# Revit family: QF_ELECTROLUXPROFESSIONAL_1LSNST_TD6-37_E
name_source: partatom
category: Attrezzature speciali
units: mm (PartAtom-declared; Revit-internal decimal feet)

## family parameters
Basato su piano di lavoro = No
Condiviso = No
Punto di calcolo locali = No
Quota connettore circolare = Usa diametro
Sempre verticale = Sì
Taglio con vuoti quando caricato = No
Tipo di parte = Normale

## types (25) — shared parameters
Depth Actual = 1560 mm  [stored 5.11811 ft]
Height Actual = 1855 mm  [stored 6.08596 ft]
Latent Heat Output = 0.0
Length Actual = 960 mm  [stored 3.14961 ft]
Modello = TD6-37
Phase = 3
Produttore = Electrolux Professional
Sensible Heat Output = 0.0
URL = www.electroluxprofessional.com
Weight = 283
zero-valued in all types: Gas KW, Prospetto di default, Steam Pounds per Hour

## per-type parameters (varying)
| type | Cycle | Descrizione | Item Number | Volts | Watts |
| 9873030098 | 60 Hz | TUMBLE DRYER TD6-37 37KG/83LB GALVA.DRUM EL 40KW 440/60/3 COMPASS PRO 6G81 SLVR/SLVR DO.LEFT REV MB STOP DISCON DMPR | 1LSPRU | 440 V | 41500 W |
| 9873030017 | 50 Hz | TUMBLE DRYER TD6-37 37KG/83LB GALVA.DRUM EL 32KW 400/50/3 COMPASS PRO 6G82 SLVR/SLVR DO.RIGHT REV STOP DISCON DMPR | 1L0G6B | 400 V | 33500 W |
| 9873030007 | 50 Hz | TUMBLE DRYER TD6-37 37KG/83LB SST DRUM EL 40KW 400/50/3N COMPASS PRO 6G81 SLVR/SLVR DO.RIGHT REV MB STOP DISCON DMPR | 1L0G61 | 400 V | 41500 W |
| 9873030012 | 50 Hz | TUMBLE DRYER TD6-37 37KG/83LB GALVA.DRUM EL 40KW 400/50/3N COMPASS PRO 6G82 SLVR/SLVR DO.RIGHT REV STOP DISCON DMPR | 1L0G66 | 400 V | 41500 W |
| 9873030042 | 50 Hz | TUMBLE DRYER TD6-37 37KG/83LB SST DRUM EL 40KW 400/50/3N COMPASS PRO 6G81 SLVR/SLVR DO.RIGHT REV MB STOP DISCON DMPR | 1L0GAY | 400 V | 41500 W |
| 9873030081 | 50 Hz | TUMBLE DRYER TD6-37 37KG/83LB SST DRUM EL 40KW 380-415/50/3N COMPASS PRO 6G81 SST/SLVR DO.LEFT REV MB STOP DISCON DMPR | 1L0GVV | 415 V | 41500 W |
| 9873030118 | 50 Hz | TUMBLE DRYER TD6-37 37KG/83LB SST DRUM EL 40KW 380-415/50/3N COMPASS PRO 6G81 SST/SST DO.LEFT REV MB STOP DISCON DMPR | 1LT6J7 | 415 V | 41500 W |
| 9873030089 | 50 Hz | TUMBLE DRYER TD6-37 37KG/83LB GALVA.DRUM EL 40KW 400/50/3N COMPASS PRO 6G81 SLVR/SLVR DO.RIGHT REV MB STOP DISCON DMPR | 1LSPKZ | 400 V | 41500 W |
| 9873030019 | 50 Hz | TUMBLE DRYER TD6-37 37KG SST DRUM EL 40KW 400/50/3N COMPASS PRO 6G82 SST/SLVR DO.RIGHT REV STOP DISCON DMPR | 1L0G6D | 400 V | 41500 W |
| 9873030009 | 50 Hz | TUMBLE DRYER TD6-37 37KG/83LB GALVA.DRUM EL 24KW 400/50/3N COMPASS PRO 6G81 SLVR/SLVR DO.RIGHT REV MB DISCON DMPR | 1L0G63 | 400 V | 25500 W |
| 9873030115 | 60 Hz | TUMBLE DRYER TD6-37 37KG/83LB SST DRUM EL 40KW 380-415/60/3N COMPASS PRO 6G82 SST/SLVR DO.RIGHT REV DISCON DMPR | 1LT65T | 415 V | 41500 W |
| 9873030069 | 50 Hz | TUMBLE DRYER TD6-37 37KG/83LB SST DRUM EL 40KW 380-415/50/3 COMPASS PRO 6G81 SLVR/SLVR DO.RIGHT REV MB STOP DISCON DMPR | 1L0GKR | 415 V | 41500 W |
| 9873030112 | 60 Hz | TUMBLE DRYER TD6-37 MARINE 37KG/83LB GALVA.DRUM EL 32KW 440/60/3 COMPASS PRO 6G82 SLVR/SLVR DO.LEFT REV STOP DISCON ... | 1L0HD9 | 440 V | 33500 W |
| 9873030014 | 50 Hz | TUMBLE DRYER TD6-37 37KG/83LB SST DRUM EL 40KW 400/50/3N COMPASS PRO 6G82 SLVR/SLVR DO.RIGHT REV STOP DISCON DMPR | 1L0G68 | 400 V | 41500 W |
| 9873030004 | 50 Hz | TUMBLE DRYER TD6-37 37KG/83LB GALVA.DRUM EL 40KW 400/50/3N COMPASS PRO 6G82 SLVR/SLVR DO.RIGHT REV DISCON DMPR | 1L0G5Y | 400 V | 41500 W |
| 9873030033 | 50 Hz | TUMBLE DRYER TD6-37 37KG/83LB SST DRUM EL 40KW 400/50/3N COMPASS PRO 6G81 SLVR/SLVR DO.LEFT REV MB STOP DISCON DMPR | 1L0G6S | 400 V | 41500 W |
| 9873030063 | 60 Hz | TUMBLE DRYER TD6-37 37KG/83LB SST DRUM EL 32KW 400/60/3 COMPASS PRO 6G82 SLVR/SLVR DO.LEFT REV STOP DISCON DMPR | 1L0GF1 | 400 V | 33500 W |
| 9873030006 | 50 Hz | TUMBLE DRYER TD6-37 37KG/83LB GALVA.DRUM EL 32KW 400/50/3N COMPASS PRO 6G81 SLVR/SLVR DO.RIGHT REV MB STOP DISCON DMPR | 1L0G60 | 400 V | 33500 W |
| 9873030076 | 60 Hz | TUMBLE DRYER TD6-37 37KG/83LB GALVA.DRUM EL 40KW 400/60/3N COMPASS PRO 6G82 SLVR/SLVR DO.RIGHT REV DISCON DMPR | 1L0GS6 | 400 V | 41500 W |
| 9873030066 | 60 Hz | TUMBLE DRYER TD6-37 37KG/83LB GALVA.DRUM EL 32KW 220/60/3 COMPASS PRO 6G82 SLVR/SLVR DO.RIGHT REV DISCON DMPR | 1L0GJE | 220 V | 33500 W |
| 9873030056 | 50 Hz | TUMBLE DRYER TD6-37 37KG/83LB SST DRUM EL 32KW 380-415/50/3N COMPASS PRO 6G82 SLVR/SLVR DO.RIGHT REV STOP DISCON DMPR | 1LA1DD | 415 V | 33500 W |
| 9873030015 | 50 Hz | TUMBLE DRYER TD6-37 37KG/83LB GALVA.DRUM EL 32KW 230/50/3 COMPASS PRO 6G81 SLVR/SLVR DO.RIGHT REV MB DISCON DMPR | 1L0G69 | 230 V | 33500 W |
| 9873030065 | 50 Hz | TUMBLE DRYER TD6-37 37KG/83LB GALVA.DRUM EL 40KW 380-415/50/3N COMPASS PRO 6G81 SLVR/SLVR DO.RIGHT REV MB DISCON DMPR | 1L0HD8 | 415 V | 41500 W |
| 9873030045 | 50 Hz | TUMBLE DRYER TD6-37 37KG/83LB GALVA.DRUM EL 40KW 400/50/3N COMPASS PRO 6G81 SLVR/SLVR DO.LEFT REV MB STOP DISCON DMPR | 1L0GCL | 400 V | 41500 W |
| 9873030020 | 50 Hz | TUMBLE DRYER TD6-37 37KG/83LB SST DRUM EL 32KW 380-415/50/3 COMPASS PRO 6G81 SST/SST DO.RIGHT REV MB STOP DISCON DMPR | 1L0G6E | 415 V | 33500 W |

note: [stored X ft] marks values corroborated as IEEE doubles in the binary element streams (Revit-internal decimal feet)

## geometry (parser evidence)
native form markers: Blend x8
no freeform markers — native parametric forms only
